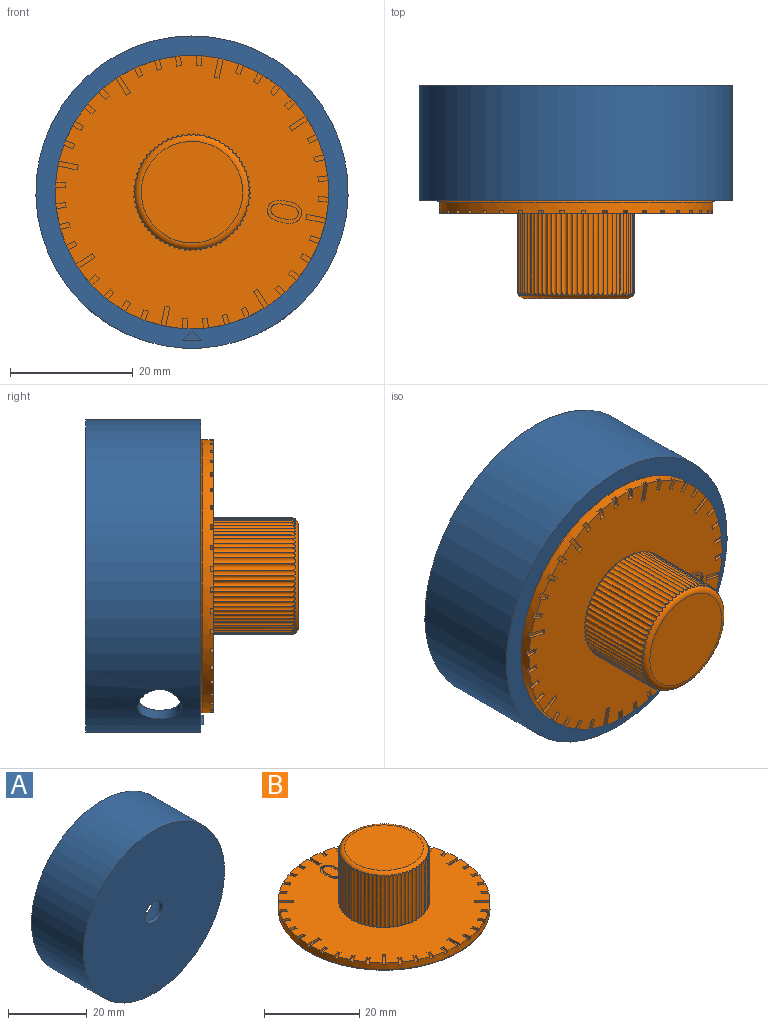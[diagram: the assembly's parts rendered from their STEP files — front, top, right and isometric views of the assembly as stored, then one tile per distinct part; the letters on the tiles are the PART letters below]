
ASSEMBLY  parts=2 mates=1
PART A: 19 faces, bbox 50.8x19.1x50.8 mm
  f0: plane 50.8x50.8mm, normal (0,-1,0), area 1992.6mm2, adj f3,f5,f15,f16,f17
  f1: plane 48.26x48.26mm, normal (0,1,0), area 1676.7mm2, adj f4,f5,f8,f10,f11,f13,f14
  f2: plane 50.8x50.8mm, normal (0,1,0), area 197.6mm2, adj f3,f4
  f3: cylinder r=25.4mm len=50.8mm, axis (0,-1,0), area 2892.6mm2, adj f0,f2,f6,f7
  f4: cylinder r=24.13mm len=48.26mm, axis (0,-1,0), area 2548.5mm2, adj f1,f2,f6,f7
  f5: cylinder r=3.17mm len=6.35mm, axis (0,1,0), area 25.3mm2, adj f0,f1
  f6: cylinder r=3.57mm len=7.14mm, axis (0,0,1), area 35.2mm2, adj f3,f4
  f7: cylinder r=3.57mm len=7.14mm, axis (0,0,1), area 35.1mm2, adj f3,f4
  f8: cylinder r=1.59mm len=15.88mm, axis (0,-1,0), area 158.3mm2, adj f1,f9
  f9: plane 3.18x3.18mm, normal (0,1,0), area 7.9mm2, adj f8
  f10: plane 22.23x1.59mm, normal (-1,0,0), area 33.2mm2, adj f1,f12,f13,f14
  f11: plane 22.23x1.59mm, normal (1,0,0), area 33.2mm2, adj f1,f12,f13,f14
  f12: plane 17.52x5.08mm, normal (0,1,0), area 89mm2, adj f10,f11,f13,f14
  f13: cylinder r=2.54mm len=5.08mm, axis (1,0,0), area 15.3mm2, adj f1,f10,f11,f12
  f14: cylinder r=2.54mm len=5.08mm, axis (-1,0,0), area 15.3mm2, adj f1,f10,f11,f12
  f15: plane 1.6x1.6mm, normal (-0.71,0,0.71), area 0.9mm2, adj f0,f16,f17,f18
  f16: plane 3.19x0.4mm, normal (0,0,-1), area 1.3mm2, adj f0,f15,f17,f18
  f17: plane 1.6x1.6mm, normal (0.71,0,0.71), area 0.9mm2, adj f0,f15,f16,f18
  f18: plane 3.19x1.6mm, normal (0,-1,0), area 2.5mm2, adj f15,f16,f17
PART B: 269 faces, bbox 48.1x48.1x19.1 mm
  f0: plane 44.45x44.45mm, normal (0,0,1), area 1200.8mm2, adj f3,f8,f9,f10,f11,f12,f13,f14
  f1: plane 3.05x1.27mm, normal (0,-1,0), area 3.9mm2, adj f237,f238,f239,f241
  f2: cylinder r=3.17mm len=6.35mm, axis (0,0,-1), area 52.5mm2, adj f7,f243,f247,f249
  f3: cylinder r=22.23mm len=44.45mm, axis (0,0,-1), area 232.2mm2, adj f0,f76,f77,f79,f80,f81,f83,f84
  f4: torus R=8.26mm, axis (0,0,1), area 73.7mm2, adj f5,f8,f9,f10,f11,f12,f13,f14
  f5: plane 16.51x16.51mm, normal (0,0,1), area 214.1mm2, adj f4
  f6: plane 5.84x5.7mm, normal (0,0,-1), area 10.8mm2, adj f243,f244,f245,f246
  f7: plane 43.94x43.94mm, normal (0,0,-1), area 1484.9mm2, adj f2,f236,f237,f238,f242,f247,f249
  f8: cylinder r=0.51mm len=13.34mm, axis (0,0,1), area 13.7mm2, adj f0,f4,f72,f73
  f9: cylinder r=0.51mm len=13.34mm, axis (0,0,1), area 13.7mm2, adj f0,f4,f70,f71
  f10: cylinder r=0.51mm len=13.34mm, axis (0,0,1), area 13.7mm2, adj f0,f4,f69,f70
  f11: cylinder r=0.51mm len=13.34mm, axis (0,0,1), area 13.7mm2, adj f0,f4,f67,f68
  f12: cylinder r=0.51mm len=13.34mm, axis (0,0,1), area 13.7mm2, adj f0,f4,f65,f66
  f13: cylinder r=0.51mm len=13.34mm, axis (0,0,1), area 13.7mm2, adj f0,f4,f63,f64
  f14: cylinder r=0.51mm len=13.34mm, axis (0,0,1), area 13.7mm2, adj f0,f4,f42,f75
  f15: cylinder r=0.51mm len=13.34mm, axis (0,0,1), area 13.7mm2, adj f0,f4,f42,f43
  f16: cylinder r=0.51mm len=13.34mm, axis (0,0,1), area 13.7mm2, adj f0,f4,f43,f44
  f17: cylinder r=0.51mm len=13.34mm, axis (0,0,1), area 13.7mm2, adj f0,f4,f44,f74
  f18: cylinder r=0.51mm len=13.34mm, axis (0,0,1), area 13.7mm2, adj f0,f4,f45,f75
  f19: cylinder r=0.64mm len=13.39mm, axis (0,0,1), area 16.6mm2, adj f0,f4,f45,f46
  f20: cylinder r=0.51mm len=13.34mm, axis (0,0,1), area 13.7mm2, adj f0,f4,f46,f47
  f21: cylinder r=0.51mm len=13.34mm, axis (0,0,1), area 13.7mm2, adj f0,f4,f47,f48
  f22: cylinder r=0.51mm len=13.34mm, axis (0,0,1), area 13.7mm2, adj f0,f4,f48,f49
  f23: cylinder r=0.51mm len=13.34mm, axis (0,0,1), area 13.7mm2, adj f0,f4,f49,f50
  f24: cylinder r=0.51mm len=13.34mm, axis (0,0,1), area 13.7mm2, adj f0,f4,f50,f51
  f25: cylinder r=0.51mm len=13.34mm, axis (0,0,1), area 13.7mm2, adj f0,f4,f51,f52
  f26: cylinder r=0.51mm len=13.34mm, axis (0,0,1), area 13.7mm2, adj f0,f4,f52,f53
  f27: cylinder r=0.51mm len=13.34mm, axis (0,0,1), area 13.7mm2, adj f0,f4,f53,f54
  f28: cylinder r=0.51mm len=13.34mm, axis (0,0,1), area 13.7mm2, adj f0,f4,f54,f55
  f29: cylinder r=0.51mm len=13.34mm, axis (0,0,1), area 13.7mm2, adj f0,f4,f55,f56
  f30: cylinder r=0.51mm len=13.34mm, axis (0,0,1), area 13.7mm2, adj f0,f4,f56,f57
  f31: cylinder r=0.51mm len=13.34mm, axis (0,0,1), area 13.7mm2, adj f0,f4,f57,f58
  f32: cylinder r=0.51mm len=13.34mm, axis (0,0,1), area 13.7mm2, adj f0,f4,f58,f59
  f33: cylinder r=0.51mm len=13.34mm, axis (0,0,1), area 13.7mm2, adj f0,f4,f59,f60
  f34: cylinder r=0.51mm len=13.34mm, axis (0,0,1), area 13.7mm2, adj f0,f4,f60,f61
  f35: cylinder r=0.51mm len=13.34mm, axis (0,0,1), area 13.7mm2, adj f0,f4,f61,f62
  f36: cylinder r=0.64mm len=13.39mm, axis (0,0,1), area 16.6mm2, adj f0,f4,f62,f63
  f37: cylinder r=0.51mm len=13.34mm, axis (0,0,1), area 13.7mm2, adj f0,f4,f64,f65
  f38: cylinder r=0.51mm len=13.34mm, axis (0,0,1), area 13.7mm2, adj f0,f4,f66,f67
  f39: cylinder r=0.51mm len=13.34mm, axis (0,0,1), area 13.7mm2, adj f0,f4,f68,f69
  f40: cylinder r=0.51mm len=13.34mm, axis (0,0,1), area 13.7mm2, adj f0,f4,f71,f72
  f41: cylinder r=0.51mm len=13.34mm, axis (0,0,1), area 13.7mm2, adj f0,f4,f73,f74
  f42: cylinder r=0.51mm len=13.34mm, axis (0,0,1), area 13.7mm2, adj f0,f4,f14,f15
  f43: cylinder r=0.51mm len=13.34mm, axis (0,0,1), area 13.7mm2, adj f0,f4,f15,f16
  f44: cylinder r=0.51mm len=13.34mm, axis (0,0,1), area 13.7mm2, adj f0,f4,f16,f17
  f45: cylinder r=0.51mm len=13.34mm, axis (0,0,1), area 13.7mm2, adj f0,f4,f18,f19
  f46: cylinder r=0.64mm len=13.39mm, axis (0,0,1), area 16.6mm2, adj f0,f4,f19,f20
  f47: cylinder r=0.51mm len=13.34mm, axis (0,0,1), area 13.7mm2, adj f0,f4,f20,f21
  f48: cylinder r=0.51mm len=13.34mm, axis (0,0,1), area 13.7mm2, adj f0,f4,f21,f22
  f49: cylinder r=0.51mm len=13.34mm, axis (0,0,1), area 13.7mm2, adj f0,f4,f22,f23
  f50: cylinder r=0.51mm len=13.34mm, axis (0,0,1), area 13.7mm2, adj f0,f4,f23,f24
  f51: cylinder r=0.51mm len=13.34mm, axis (0,0,1), area 13.7mm2, adj f0,f4,f24,f25
  f52: cylinder r=0.51mm len=13.34mm, axis (0,0,1), area 13.7mm2, adj f0,f4,f25,f26
  f53: cylinder r=0.51mm len=13.34mm, axis (0,0,1), area 13.7mm2, adj f0,f4,f26,f27
  f54: cylinder r=0.51mm len=13.34mm, axis (0,0,1), area 13.7mm2, adj f0,f4,f27,f28
  f55: cylinder r=0.51mm len=13.34mm, axis (0,0,1), area 13.7mm2, adj f0,f4,f28,f29
  f56: cylinder r=0.51mm len=13.34mm, axis (0,0,1), area 13.7mm2, adj f0,f4,f29,f30
  f57: cylinder r=0.51mm len=13.34mm, axis (0,0,1), area 13.7mm2, adj f0,f4,f30,f31
  f58: cylinder r=0.51mm len=13.34mm, axis (0,0,1), area 13.7mm2, adj f0,f4,f31,f32
  f59: cylinder r=0.51mm len=13.34mm, axis (0,0,1), area 13.7mm2, adj f0,f4,f32,f33
  f60: cylinder r=0.51mm len=13.34mm, axis (0,0,1), area 13.7mm2, adj f0,f4,f33,f34
  f61: cylinder r=0.51mm len=13.34mm, axis (0,0,1), area 13.7mm2, adj f0,f4,f34,f35
  f62: cylinder r=0.51mm len=13.34mm, axis (0,0,1), area 13.7mm2, adj f0,f4,f35,f36
  f63: cylinder r=0.64mm len=13.39mm, axis (0,0,1), area 16.6mm2, adj f0,f4,f13,f36
  f64: cylinder r=0.51mm len=13.34mm, axis (0,0,1), area 13.7mm2, adj f0,f4,f13,f37
  f65: cylinder r=0.51mm len=13.34mm, axis (0,0,1), area 13.7mm2, adj f0,f4,f12,f37
  f66: cylinder r=0.51mm len=13.34mm, axis (0,0,1), area 13.7mm2, adj f0,f4,f12,f38
  f67: cylinder r=0.51mm len=13.34mm, axis (0,0,1), area 13.7mm2, adj f0,f4,f11,f38
  f68: cylinder r=0.51mm len=13.34mm, axis (0,0,1), area 13.7mm2, adj f0,f4,f11,f39
  f69: cylinder r=0.51mm len=13.34mm, axis (0,0,1), area 13.7mm2, adj f0,f4,f10,f39
  f70: cylinder r=0.51mm len=13.34mm, axis (0,0,1), area 13.7mm2, adj f0,f4,f9,f10
  f71: cylinder r=0.51mm len=13.34mm, axis (0,0,1), area 13.7mm2, adj f0,f4,f9,f40
  f72: cylinder r=0.51mm len=13.34mm, axis (0,0,1), area 13.7mm2, adj f0,f4,f8,f40
  f73: cylinder r=0.51mm len=13.34mm, axis (0,0,1), area 13.7mm2, adj f0,f4,f8,f41
  f74: cylinder r=0.51mm len=13.34mm, axis (0,0,1), area 13.7mm2, adj f0,f4,f17,f41
  f75: cylinder r=0.51mm len=13.34mm, axis (0,0,1), area 13.7mm2, adj f0,f4,f14,f18
  f76: plane 3.18x0.51mm, normal (-1,0,0), area 1.6mm2, adj f0,f3,f78,f79
  f77: plane 3.18x0.51mm, normal (1,0,0), area 1.6mm2, adj f0,f3,f78,f79
  f78: plane 0.79x0.51mm, normal (0,1,0), area 0.4mm2, adj f0,f76,f77,f79
  f79: plane 3.18x0.8mm, normal (0,0,1), area 2.5mm2, adj f3,f76,f77,f78
  f80: plane 1.57x0.51mm, normal (-0.99,-0.16,0), area 0.8mm2, adj f0,f3,f82,f83
  f81: plane 1.57x0.51mm, normal (0.99,0.16,0), area 0.8mm2, adj f0,f3,f82,f83
  f82: plane 0.78x0.51mm, normal (-0.16,0.99,0), area 0.4mm2, adj f0,f80,f81,f83
  f83: plane 1.7x1.04mm, normal (0,0,1), area 1.3mm2, adj f3,f80,f81,f82
  f84: plane 1.51x0.51mm, normal (-0.95,-0.31,0), area 0.8mm2, adj f0,f3,f86,f87
  f85: plane 1.51x0.51mm, normal (0.95,0.31,0), area 0.8mm2, adj f0,f3,f86,f87
  f86: plane 0.76x0.51mm, normal (-0.31,0.95,0), area 0.4mm2, adj f0,f84,f85,f87
  f87: plane 1.76x1.25mm, normal (0,0,1), area 1.3mm2, adj f3,f84,f85,f86
  f88: plane 1.42x0.72mm, normal (-0.89,-0.45,0), area 0.8mm2, adj f0,f3,f90,f91
  f89: plane 1.42x0.72mm, normal (0.89,0.45,0), area 0.8mm2, adj f0,f3,f90,f91
  f90: plane 0.71x0.51mm, normal (-0.45,0.89,0), area 0.4mm2, adj f0,f88,f89,f91
  f91: plane 1.78x1.44mm, normal (0,0,1), area 1.3mm2, adj f3,f88,f89,f90
  f92: plane 1.29x0.93mm, normal (-0.59,-0.81,0), area 0.8mm2, adj f0,f3,f94,f95
  f93: plane 1.29x0.93mm, normal (0.59,0.81,0), area 0.8mm2, adj f0,f3,f94,f95
  f94: plane 0.64x0.51mm, normal (-0.81,0.59,0), area 0.4mm2, adj f0,f92,f93,f95
  f95: plane 1.76x1.58mm, normal (0,0,1), area 1.3mm2, adj f3,f92,f93,f94
  f96: plane 2.25x2.25mm, normal (-0.71,-0.71,0), area 1.6mm2, adj f0,f3,f98,f99
  f97: plane 2.25x2.25mm, normal (0.71,0.71,0), area 1.6mm2, adj f0,f3,f98,f99
  f98: plane 0.56x0.56mm, normal (-0.71,0.71,0), area 0.4mm2, adj f0,f96,f97,f99
  f99: plane 2.81x2.81mm, normal (0,0,1), area 2.5mm2, adj f3,f96,f97,f98
  f100: plane 1.57x0.51mm, normal (-0.16,-0.99,0), area 0.8mm2, adj f0,f3,f102,f103
  f101: plane 1.57x0.51mm, normal (0.16,0.99,0), area 0.8mm2, adj f0,f3,f102,f103
  f102: plane 0.78x0.51mm, normal (-0.99,0.16,0), area 0.4mm2, adj f0,f100,f101,f103
  f103: plane 1.7x1.04mm, normal (0,0,1), area 1.3mm2, adj f3,f100,f101,f102
  f104: plane 1.29x0.93mm, normal (-0.81,-0.59,0), area 0.8mm2, adj f0,f3,f106,f107
  f105: plane 1.29x0.93mm, normal (0.81,0.59,0), area 0.8mm2, adj f0,f3,f106,f107
  f106: plane 0.64x0.51mm, normal (-0.59,0.81,0), area 0.4mm2, adj f0,f104,f105,f107
  f107: plane 1.76x1.58mm, normal (0,0,1), area 1.3mm2, adj f3,f104,f105,f106
  f108: plane 1.29x0.93mm, normal (0.59,-0.81,0), area 0.8mm2, adj f0,f3,f109,f111
  f109: plane 0.64x0.51mm, normal (0.81,0.59,0), area 0.4mm2, adj f0,f108,f110,f111
  f110: plane 1.29x0.93mm, normal (-0.59,0.81,0), area 0.8mm2, adj f0,f3,f109,f111
  f111: plane 1.76x1.58mm, normal (0,0,1), area 1.3mm2, adj f3,f108,f109,f110
  f112: plane 1.42x0.72mm, normal (0.45,-0.89,0), area 0.8mm2, adj f0,f3,f113,f115
  f113: plane 0.71x0.51mm, normal (0.89,0.45,0), area 0.4mm2, adj f0,f112,f114,f115
  f114: plane 1.42x0.72mm, normal (-0.45,0.89,0), area 0.8mm2, adj f0,f3,f113,f115
  f115: plane 1.78x1.44mm, normal (0,0,1), area 1.3mm2, adj f3,f112,f113,f114
  f116: plane 1.51x0.51mm, normal (0.31,-0.95,0), area 0.8mm2, adj f0,f3,f117,f119
  f117: plane 0.76x0.51mm, normal (0.95,0.31,0), area 0.4mm2, adj f0,f116,f118,f119
  f118: plane 1.51x0.51mm, normal (-0.31,0.95,0), area 0.8mm2, adj f0,f3,f117,f119
  f119: plane 1.76x1.25mm, normal (0,0,1), area 1.3mm2, adj f3,f116,f117,f118
  f120: plane 1.29x0.93mm, normal (0.81,-0.59,0), area 0.8mm2, adj f0,f3,f121,f123
  f121: plane 0.64x0.51mm, normal (0.59,0.81,0), area 0.4mm2, adj f0,f120,f122,f123
  f122: plane 1.29x0.93mm, normal (-0.81,0.59,0), area 0.8mm2, adj f0,f3,f121,f123
  f123: plane 1.76x1.58mm, normal (0,0,1), area 1.3mm2, adj f3,f120,f121,f122
  f124: plane 2.25x2.25mm, normal (0.71,-0.71,0), area 1.6mm2, adj f0,f3,f125,f127
  f125: plane 0.56x0.56mm, normal (0.71,0.71,0), area 0.4mm2, adj f0,f124,f126,f127
  f126: plane 2.25x2.25mm, normal (-0.71,0.71,0), area 1.6mm2, adj f0,f3,f125,f127
  f127: plane 2.81x2.81mm, normal (0,0,1), area 2.5mm2, adj f3,f124,f125,f126
  f128: plane 1.42x0.72mm, normal (0.89,-0.45,0), area 0.8mm2, adj f0,f3,f129,f131
  f129: plane 0.71x0.51mm, normal (0.45,0.89,0), area 0.4mm2, adj f0,f128,f130,f131
  f130: plane 1.42x0.72mm, normal (-0.89,0.45,0), area 0.8mm2, adj f0,f3,f129,f131
  f131: plane 1.78x1.44mm, normal (0,0,1), area 1.3mm2, adj f3,f128,f129,f130
  f132: plane 1.51x0.51mm, normal (0.95,-0.31,0), area 0.8mm2, adj f0,f3,f133,f135
  f133: plane 0.76x0.51mm, normal (0.31,0.95,0), area 0.4mm2, adj f0,f132,f134,f135
  f134: plane 1.51x0.51mm, normal (-0.95,0.31,0), area 0.8mm2, adj f0,f3,f133,f135
  f135: plane 1.76x1.25mm, normal (0,0,1), area 1.3mm2, adj f3,f132,f133,f134
  f136: plane 1.57x0.51mm, normal (0.99,-0.16,0), area 0.8mm2, adj f0,f3,f137,f139
  f137: plane 0.78x0.51mm, normal (0.16,0.99,0), area 0.4mm2, adj f0,f136,f138,f139
  f138: plane 1.57x0.51mm, normal (-0.99,0.16,0), area 0.8mm2, adj f0,f3,f137,f139
  f139: plane 1.7x1.04mm, normal (0,0,1), area 1.3mm2, adj f3,f136,f137,f138
  f140: plane 1.57x0.51mm, normal (0.16,-0.99,0), area 0.8mm2, adj f0,f3,f141,f143
  f141: plane 0.78x0.51mm, normal (0.99,0.16,0), area 0.4mm2, adj f0,f140,f142,f143
  f142: plane 1.57x0.51mm, normal (-0.16,0.99,0), area 0.8mm2, adj f0,f3,f141,f143
  f143: plane 1.7x1.04mm, normal (0,0,1), area 1.3mm2, adj f3,f140,f141,f142
  f144: plane 3.18x0.51mm, normal (0,-1,0), area 1.6mm2, adj f0,f3,f145,f147
  f145: plane 0.79x0.51mm, normal (1,0,0), area 0.4mm2, adj f0,f144,f146,f147
  f146: plane 3.18x0.51mm, normal (0,1,0), area 1.6mm2, adj f0,f3,f145,f147
  f147: plane 3.18x0.8mm, normal (0,0,1), area 2.5mm2, adj f3,f144,f145,f146
  f148: plane 1.57x0.51mm, normal (0.16,0.99,0), area 0.8mm2, adj f0,f3,f150,f151
  f149: plane 1.57x0.51mm, normal (-0.16,-0.99,0), area 0.8mm2, adj f0,f3,f150,f151
  f150: plane 0.78x0.51mm, normal (0.99,-0.16,0), area 0.4mm2, adj f0,f148,f149,f151
  f151: plane 1.7x1.04mm, normal (0,0,1), area 1.3mm2, adj f3,f148,f149,f150
  f152: plane 1.51x0.51mm, normal (0.31,0.95,0), area 0.8mm2, adj f0,f3,f154,f155
  f153: plane 1.51x0.51mm, normal (-0.31,-0.95,0), area 0.8mm2, adj f0,f3,f154,f155
  f154: plane 0.76x0.51mm, normal (0.95,-0.31,0), area 0.4mm2, adj f0,f152,f153,f155
  f155: plane 1.76x1.25mm, normal (0,0,1), area 1.3mm2, adj f3,f152,f153,f154
  f156: plane 1.42x0.72mm, normal (0.45,0.89,0), area 0.8mm2, adj f0,f3,f158,f159
  f157: plane 1.42x0.72mm, normal (-0.45,-0.89,0), area 0.8mm2, adj f0,f3,f158,f159
  f158: plane 0.71x0.51mm, normal (0.89,-0.45,0), area 0.4mm2, adj f0,f156,f157,f159
  f159: plane 1.78x1.44mm, normal (0,0,1), area 1.3mm2, adj f3,f156,f157,f158
  f160: plane 1.29x0.93mm, normal (0.59,0.81,0), area 0.8mm2, adj f0,f3,f162,f163
  f161: plane 1.29x0.93mm, normal (-0.59,-0.81,0), area 0.8mm2, adj f0,f3,f162,f163
  f162: plane 0.64x0.51mm, normal (0.81,-0.59,0), area 0.4mm2, adj f0,f160,f161,f163
  f163: plane 1.76x1.58mm, normal (0,0,1), area 1.3mm2, adj f3,f160,f161,f162
  f164: plane 2.25x2.25mm, normal (0.71,0.71,0), area 1.6mm2, adj f0,f3,f166,f167
  f165: plane 2.25x2.25mm, normal (-0.71,-0.71,0), area 1.6mm2, adj f0,f3,f166,f167
  f166: plane 0.56x0.56mm, normal (0.71,-0.71,0), area 0.4mm2, adj f0,f164,f165,f167
  f167: plane 2.81x2.81mm, normal (0,0,1), area 2.5mm2, adj f3,f164,f165,f166
  f168: plane 1.29x0.93mm, normal (0.81,0.59,0), area 0.8mm2, adj f0,f3,f170,f171
  f169: plane 1.29x0.93mm, normal (-0.81,-0.59,0), area 0.8mm2, adj f0,f3,f170,f171
  f170: plane 0.64x0.51mm, normal (0.59,-0.81,0), area 0.4mm2, adj f0,f168,f169,f171
  f171: plane 1.76x1.58mm, normal (0,0,1), area 1.3mm2, adj f3,f168,f169,f170
  f172: plane 1.42x0.72mm, normal (0.89,0.45,0), area 0.8mm2, adj f0,f3,f174,f175
  f173: plane 1.42x0.72mm, normal (-0.89,-0.45,0), area 0.8mm2, adj f0,f3,f174,f175
  f174: plane 0.71x0.51mm, normal (0.45,-0.89,0), area 0.4mm2, adj f0,f172,f173,f175
  f175: plane 1.78x1.44mm, normal (0,0,1), area 1.3mm2, adj f3,f172,f173,f174
  f176: plane 1.51x0.51mm, normal (-0.95,-0.31,0), area 0.8mm2, adj f0,f3,f177,f179
  f177: plane 0.76x0.51mm, normal (0.31,-0.95,0), area 0.4mm2, adj f0,f176,f178,f179
  f178: plane 1.51x0.51mm, normal (0.95,0.31,0), area 0.8mm2, adj f0,f3,f177,f179
  f179: plane 1.76x1.25mm, normal (0,0,1), area 1.3mm2, adj f3,f176,f177,f178
  f180: plane 1.57x0.51mm, normal (0.99,0.16,0), area 0.8mm2, adj f0,f3,f182,f183
  f181: plane 1.57x0.51mm, normal (-0.99,-0.16,0), area 0.8mm2, adj f0,f3,f182,f183
  f182: plane 0.78x0.51mm, normal (0.16,-0.99,0), area 0.4mm2, adj f0,f180,f181,f183
  f183: plane 1.7x1.04mm, normal (0,0,1), area 1.3mm2, adj f3,f180,f181,f182
  f184: plane 0.79x0.51mm, normal (0,-1,0), area 0.4mm2, adj f0,f185,f186,f187
  f185: plane 3.18x0.51mm, normal (1,0,0), area 1.6mm2, adj f0,f3,f184,f187
  f186: plane 3.18x0.51mm, normal (-1,0,0), area 1.6mm2, adj f0,f3,f184,f187
  f187: plane 3.18x0.8mm, normal (0,0,1), area 2.5mm2, adj f3,f184,f185,f186
  f188: plane 1.57x0.51mm, normal (-0.99,0.16,0), area 0.8mm2, adj f0,f3,f189,f191
  f189: plane 0.78x0.51mm, normal (-0.16,-0.99,0), area 0.4mm2, adj f0,f188,f190,f191
  f190: plane 1.57x0.51mm, normal (0.99,-0.16,0), area 0.8mm2, adj f0,f3,f189,f191
  f191: plane 1.7x1.04mm, normal (0,0,1), area 1.3mm2, adj f3,f188,f189,f190
  f192: plane 1.51x0.51mm, normal (-0.95,0.31,0), area 0.8mm2, adj f0,f3,f193,f195
  f193: plane 0.76x0.51mm, normal (-0.31,-0.95,0), area 0.4mm2, adj f0,f192,f194,f195
  f194: plane 1.51x0.51mm, normal (0.95,-0.31,0), area 0.8mm2, adj f0,f3,f193,f195
  f195: plane 1.76x1.25mm, normal (0,0,1), area 1.3mm2, adj f3,f192,f193,f194
  f196: plane 1.42x0.72mm, normal (-0.89,0.45,0), area 0.8mm2, adj f0,f3,f197,f199
  f197: plane 0.71x0.51mm, normal (-0.45,-0.89,0), area 0.4mm2, adj f0,f196,f198,f199
  f198: plane 1.42x0.72mm, normal (0.89,-0.45,0), area 0.8mm2, adj f0,f3,f197,f199
  f199: plane 1.78x1.44mm, normal (0,0,1), area 1.3mm2, adj f3,f196,f197,f198
  f200: plane 1.29x0.93mm, normal (-0.81,0.59,0), area 0.8mm2, adj f0,f3,f201,f203
  f201: plane 0.64x0.51mm, normal (-0.59,-0.81,0), area 0.4mm2, adj f0,f200,f202,f203
  f202: plane 1.29x0.93mm, normal (0.81,-0.59,0), area 0.8mm2, adj f0,f3,f201,f203
  f203: plane 1.76x1.58mm, normal (0,0,1), area 1.3mm2, adj f3,f200,f201,f202
  f204: plane 2.25x2.25mm, normal (-0.71,0.71,0), area 1.6mm2, adj f0,f3,f205,f207
  f205: plane 0.56x0.56mm, normal (-0.71,-0.71,0), area 0.4mm2, adj f0,f204,f206,f207
  f206: plane 2.25x2.25mm, normal (0.71,-0.71,0), area 1.6mm2, adj f0,f3,f205,f207
  f207: plane 2.81x2.81mm, normal (0,0,1), area 2.5mm2, adj f3,f204,f205,f206
  f208: plane 1.29x0.93mm, normal (-0.59,0.81,0), area 0.8mm2, adj f0,f3,f209,f211
  f209: plane 0.64x0.51mm, normal (-0.81,-0.59,0), area 0.4mm2, adj f0,f208,f210,f211
  f210: plane 1.29x0.93mm, normal (0.59,-0.81,0), area 0.8mm2, adj f0,f3,f209,f211
  f211: plane 1.76x1.58mm, normal (0,0,1), area 1.3mm2, adj f3,f208,f209,f210
  f212: plane 1.42x0.72mm, normal (-0.45,0.89,0), area 0.8mm2, adj f0,f3,f213,f215
  f213: plane 0.71x0.51mm, normal (-0.89,-0.45,0), area 0.4mm2, adj f0,f212,f214,f215
  f214: plane 1.42x0.72mm, normal (0.45,-0.89,0), area 0.8mm2, adj f0,f3,f213,f215
  f215: plane 1.78x1.44mm, normal (0,0,1), area 1.3mm2, adj f3,f212,f213,f214
  f216: plane 0.76x0.51mm, normal (-0.95,-0.31,0), area 0.4mm2, adj f0,f217,f218,f219
  f217: plane 1.51x0.51mm, normal (0.31,-0.95,0), area 0.8mm2, adj f0,f3,f216,f219
  f218: plane 1.51x0.51mm, normal (-0.31,0.95,0), area 0.8mm2, adj f0,f3,f216,f219
  f219: plane 1.76x1.25mm, normal (0,0,1), area 1.3mm2, adj f3,f216,f217,f218
  f220: plane 0.78x0.51mm, normal (-0.99,-0.16,0), area 0.4mm2, adj f0,f221,f222,f223
  f221: plane 1.57x0.51mm, normal (0.16,-0.99,0), area 0.8mm2, adj f0,f3,f220,f223
  f222: plane 1.57x0.51mm, normal (-0.16,0.99,0), area 0.8mm2, adj f0,f3,f220,f223
  f223: plane 1.7x1.04mm, normal (0,0,1), area 1.3mm2, adj f3,f220,f221,f222
  f224: plane 3.18x0.51mm, normal (0,-1,0), area 1.6mm2, adj f0,f3,f226,f227
  f225: plane 3.18x0.51mm, normal (0,1,0), area 1.6mm2, adj f0,f3,f226,f227
  f226: plane 0.79x0.51mm, normal (-1,0,0), area 0.4mm2, adj f0,f224,f225,f227
  f227: plane 3.18x0.8mm, normal (0,0,1), area 2.5mm2, adj f3,f224,f225,f226
  f228: plane 1.51x0.51mm, normal (-0.31,-0.95,0), area 0.8mm2, adj f0,f3,f230,f231
  f229: plane 1.51x0.51mm, normal (0.31,0.95,0), area 0.8mm2, adj f0,f3,f230,f231
  f230: plane 0.76x0.51mm, normal (-0.95,0.31,0), area 0.4mm2, adj f0,f228,f229,f231
  f231: plane 1.76x1.25mm, normal (0,0,1), area 1.3mm2, adj f3,f228,f229,f230
  f232: plane 1.42x0.72mm, normal (-0.45,-0.89,0), area 0.8mm2, adj f0,f3,f234,f235
  f233: plane 1.42x0.72mm, normal (0.45,0.89,0), area 0.8mm2, adj f0,f3,f234,f235
  f234: plane 0.71x0.51mm, normal (-0.89,0.45,0), area 0.4mm2, adj f0,f232,f233,f235
  f235: plane 1.78x1.44mm, normal (0,0,1), area 1.3mm2, adj f3,f232,f233,f234
  f236: cylinder r=3.17mm len=12.57mm, axis (0,0,-1), area 16.1mm2, adj f7,f237,f238,f239
  f237: plane 15.49x2.35mm, normal (1,0,0), area 22.6mm2, adj f1,f7,f236,f239,f240,f241,f244,f247
  f238: plane 15.49x2.35mm, normal (-1,0,0), area 22.6mm2, adj f1,f7,f236,f239,f240,f241,f245,f249
  f239: plane 2.42x1.27mm, normal (0,0,-1), area 3mm2, adj f1,f236,f237,f238
  f240: cylinder r=1.91mm len=12.45mm, axis (0,0,-1), area 132.9mm2, adj f237,f238,f241,f246
  f241: plane 3.81x3.7mm, normal (0,0,-1), area 10mm2, adj f1,f237,f238,f240
  f242: torus R=21.97mm, axis (0,0,-1), area 55.5mm2, adj f3,f7
  f243: torus R=2.92mm, axis (0,0,-1), area 7mm2, adj f2,f6,f248,f250
  f244: cylinder r=0.25mm len=0.99mm, axis (0,-1,0), area 0.4mm2, adj f6,f237,f246,f248
  f245: cylinder r=0.25mm len=0.99mm, axis (0,1,0), area 0.4mm2, adj f6,f238,f246,f250
  f246: torus R=2.16mm, axis (0,0,-1), area 4.4mm2, adj f6,f240,f244,f245
  f247: cylinder r=0.25mm len=2.92mm, axis (0,0,-1), area 1.4mm2, adj f2,f7,f237,f248
  f248: sphere r=0.25mm, area 0.1mm2, adj f243,f244,f247
  f249: cylinder r=0.25mm len=2.92mm, axis (0,0,-1), area 1.4mm2, adj f2,f7,f238,f250
  f250: sphere r=0.25mm, area 0.1mm2, adj f243,f245,f249
  f251: extruded ~1.71x0.28mm, area 0.4mm2, adj f252,f266,f267,f268
  f252: extruded ~1.71x0.28mm, area 0.4mm2, adj f251,f253,f267,f268
  f253: extruded ~0.88x0.53mm, area 0.3mm2, adj f252,f254,f267,f268
  f254: extruded ~0.89x0.54mm, area 0.3mm2, adj f253,f255,f267,f268
  f255: extruded ~1.7x0.27mm, area 0.4mm2, adj f254,f256,f267,f268
  f256: extruded ~1.7x0.27mm, area 0.4mm2, adj f255,f257,f267,f268
  f257: extruded ~0.89x0.54mm, area 0.3mm2, adj f256,f266,f267,f268
  f258: extruded ~2.09x0.44mm, area 0.5mm2, adj f0,f259,f265,f267
  f259: extruded ~2.06x0.46mm, area 0.5mm2, adj f0,f258,f260,f267
  f260: extruded ~1.33x0.71mm, area 0.4mm2, adj f0,f259,f261,f267
  f261: extruded ~1.34x0.68mm, area 0.4mm2, adj f0,f260,f262,f267
  f262: extruded ~2.09x0.44mm, area 0.5mm2, adj f0,f261,f263,f267
  f263: extruded ~2.07x0.45mm, area 0.5mm2, adj f0,f262,f264,f267
  f264: extruded ~1.32x0.71mm, area 0.4mm2, adj f0,f263,f265,f267
  f265: extruded ~1.35x0.69mm, area 0.4mm2, adj f0,f258,f264,f267
  f266: extruded ~0.88x0.54mm, area 0.3mm2, adj f251,f257,f267,f268
  f267: plane 5.55x3.56mm, normal (0,0,1), area 7.7mm2, adj f251,f252,f253,f254,f255,f256,f257,f258
  f268: plane 4.49x2.32mm, normal (0,0,1), area 8.8mm2, adj f251,f252,f253,f254,f255,f256,f257,f266
PLACE A t=(-16.56,-10.92,9.81)mm fixed
PLACE B rot(axis=(0.5,0.61,-0.61),127.2deg) t=(-16.56,-9.01,9.81)mm
MATE revolute B.f2 <-> A.f3  axis (0,1,0) through (-16.56,-12.19,9.81)mm
